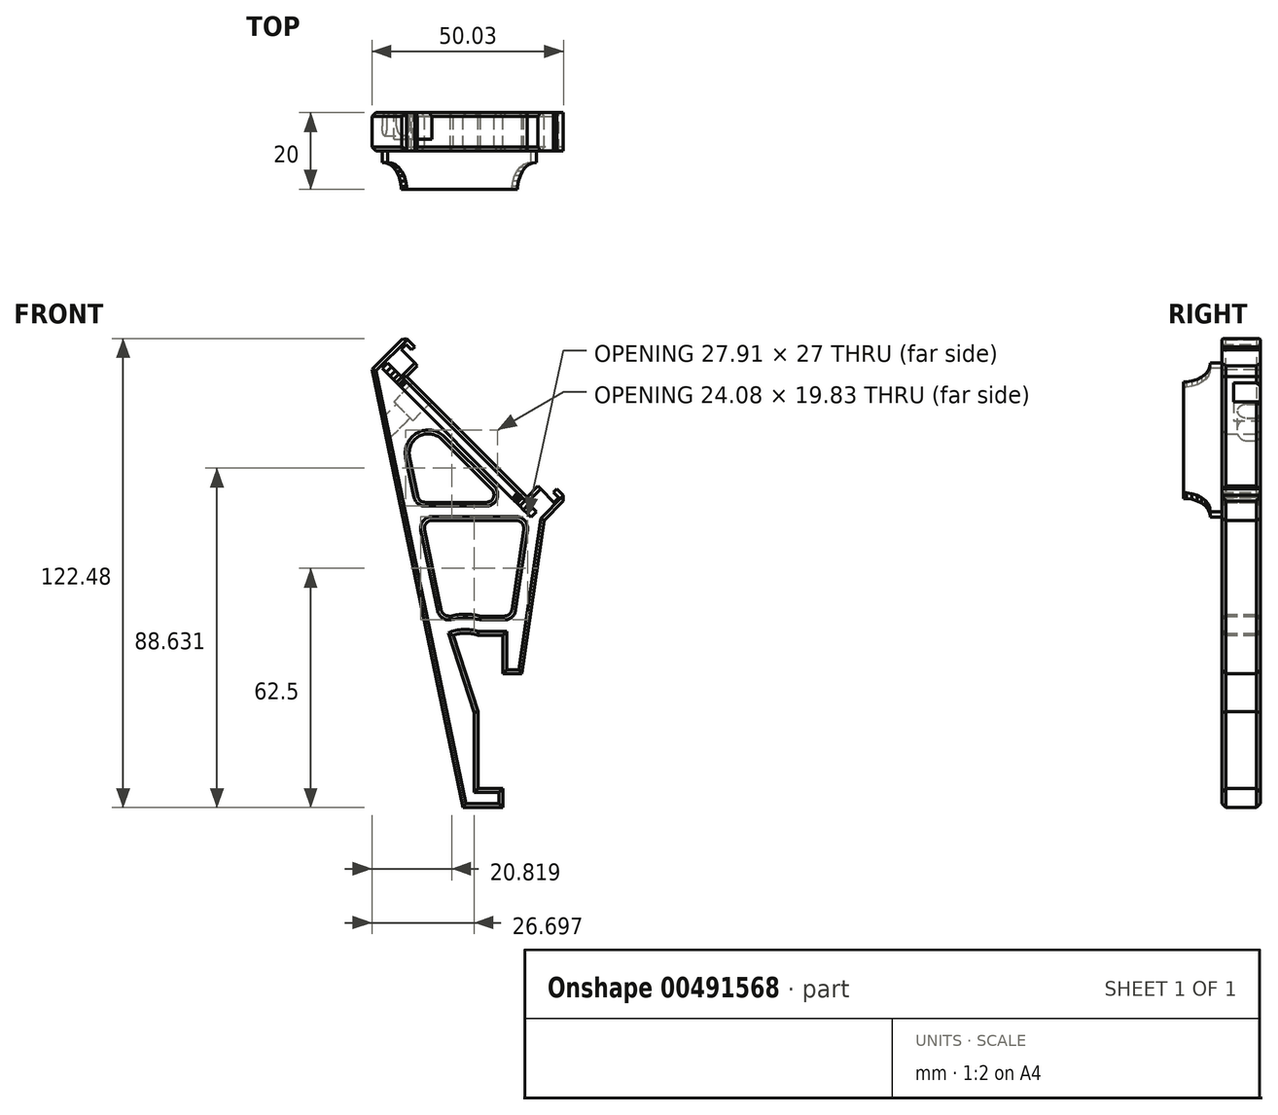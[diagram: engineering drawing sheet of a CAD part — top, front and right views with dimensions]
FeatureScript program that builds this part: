
annotation { "Feature Type Name" : "Feature", "Feature Type Description" : "" }
export const myFeature = defineFeature(function(context is Context, id is Id, definition is map)
    precondition{}
    {
        {
            assignVariable(context, id + "F0", {"name" : "contrastKnobSize", "anyValue" : 7});
        }
        {
            var Q0;
            Q0=qCreatedBy(makeId("Front.planeOp"),FACE);
            var sketch = newSketch(context, id + "F1", { "sketchPlane" : qUnion([Q0])});
            skLineSegment(sketch, "E0", {"start": v(39.1, -18.74) * mm, "end": v(39.1, -17.22) * mm});
            skLineSegment(sketch, "E1", {"start": v(39.1, -17.22) * mm, "end": v(37.38, -15.5) * mm});
            skLineSegment(sketch, "E2", {"start": v(37.38, -15.5) * mm, "end": v(36.53, -16.35) * mm});
            skLineSegment(sketch, "E3", {"start": v(36.53, -16.35) * mm, "end": v(37.94, -17.77) * mm});
            skLineSegment(sketch, "E4", {"start": v(37.94, -17.77) * mm, "end": v(36.67, -19.04) * mm});
            skLineSegment(sketch, "E5", {"start": v(36.67, -19.04) * mm, "end": v(32.43, -14.8) * mm});
            skLineSegment(sketch, "E6", {"start": v(32.43, -14.8) * mm, "end": v(29.6, -17.63) * mm});
            skLineSegment(sketch, "E7", {"start": v(29.6, -17.63) * mm, "end": v(-1.87, 13.84) * mm});
            skLineSegment(sketch, "E8", {"start": v(-1.87, 13.84) * mm, "end": v(0.96, 16.67) * mm});
            skLineSegment(sketch, "E9", {"start": v(0.96, 16.67) * mm, "end": v(-3.28, 20.91) * mm});
            skLineSegment(sketch, "E10", {"start": v(-3.28, 20.91) * mm, "end": v(-2, 22.18) * mm});
            skLineSegment(sketch, "E11", {"start": v(-2, 22.18) * mm, "end": v(-0.6, 20.77) * mm});
            skLineSegment(sketch, "E12", {"start": v(-0.6, 20.77) * mm, "end": v(0.26, 21.62) * mm});
            skLineSegment(sketch, "E13", {"start": v(0.26, 21.62) * mm, "end": v(-1.87, 23.74) * mm});
            skLineSegment(sketch, "E14", {"start": v(-3.15, 23.46) * mm, "end": v(-10.93, 15.68) * mm});
            skLineSegment(sketch, "E15", {"start": v(34.1, -23.74) * mm, "end": v(39.1, -18.74) * mm});
            skLineSegment(sketch, "E16", {"start": v(11.52, -23.74) * mm, "end": v(18.05, -23.74) * mm});
            skLineSegment(sketch, "E17.0", {"start": v(-3.93, -19.02) * mm, "end": v(-3.73, -19.02) * mm});
            skPoint(sketch, "E18.visualSharp", {"position": v(-11.06, -23.74) * mm});
            skLineSegment(sketch, "E18.filletArc", {"start": v(-11.06, -23.74) * mm, "end": v(-11.06, -23.74) * mm});
            skLineSegment(sketch, "E19", {"start": v(34.1, -23.74) * mm, "end": v(34.1, -53.74) * mm, "construction": true});
            skLineSegment(sketch, "E20", {"start": v(34.1, -53.74) * mm, "end": v(34.1, -73.74) * mm, "construction": true});
            skLineSegment(sketch, "E21", {"start": v(7.34, -2.6) * mm, "end": v(20.36, -15.6) * mm});
            skLineSegment(sketch, "E22.trimOffspring", {"start": v(-3.73, -19.02) * mm, "end": v(-3.93, -19.02) * mm, "construction": true});
            skLineSegment(sketch, "E23.trimOffspring", {"start": v(1.05, -17.43) * mm, "end": v(-1.09, -7.15) * mm});
            skLineSegment(sketch, "E24", {"start": v(3, -19.02) * mm, "end": v(18.94, -19.02) * mm});
            skPoint(sketch, "E25.visualSharp", {"position": v(1.38, -19.02) * mm});
            skArc(sketch, "E25.filletArc", {"start": v(1.05, -17.43) * mm, "mid": v(1.74, -18.58) * mm, "end": v(3, -19.02) * mm});
            skPoint(sketch, "E26.visualSharp", {"position": v(23.77, -19.02) * mm});
            skArc(sketch, "E26.filletArc", {"start": v(18.94, -19.02) * mm, "mid": v(20.8, -17.79) * mm, "end": v(20.36, -15.6) * mm});
            skLineSegment(sketch, "E27.trimOffspring", {"start": v(23.05, -23.74) * mm, "end": v(26.73, -23.74) * mm});
            skPoint(sketch, "E28.0.midPoint", {"position": v(0, 0.45) * mm});
            skLineSegment(sketch, "E29", {"start": v(-1.87, 23.74) * mm, "end": v(-3.15, 23.46) * mm});
            skArc(sketch, "E30.filletArc", {"start": v(7.34, -2.6) * mm, "mid": v(1.43, -1.73) * mm, "end": v(-1.09, -7.15) * mm});
            skLineSegment(sketch, "E31", {"start": v(23.05, -23.74) * mm, "end": v(18.05, -23.74) * mm});
            skLineSegment(sketch, "E32", {"start": v(11.52, -23.74) * mm, "end": v(5.02, -23.74) * mm});
            skLineSegment(sketch, "E33", {"start": v(5.02, -23.74) * mm, "end": v(4.81, -23.74) * mm});
            skLineSegment(sketch, "E34.trimOffspring", {"start": v(-2.75, -23.74) * mm, "end": v(-10.93, 15.68) * mm});
            skPoint(sketch, "E35.start.orphan", {"position": v(11.52, -53.74) * mm});
            skLineSegment(sketch, "E36", {"start": v(34.1, -73.74) * mm, "end": v(34.1, -93.74) * mm, "construction": true});
            skLineSegment(sketch, "E37", {"start": v(-2.75, -23.74) * mm, "end": v(12.81, -98.74) * mm});
            skLineSegment(sketch, "E38", {"start": v(34.1, -93.74) * mm, "end": v(16.77, -93.74) * mm, "construction": true});
            skLineSegment(sketch, "E39", {"start": v(16.77, -93.74) * mm, "end": v(16.77, -73.74) * mm});
            skLineSegment(sketch, "E40", {"start": v(16.77, -73.74) * mm, "end": v(10.28, -53.74) * mm});
            skPoint(sketch, "E41.orphan", {"position": v(16.77, -53.74) * mm});
            skLineSegment(sketch, "E42", {"start": v(16.77, -53.74) * mm, "end": v(23.27, -53.74) * mm});
            skLineSegment(sketch, "E43", {"start": v(23.27, -53.74) * mm, "end": v(23.27, -63.74) * mm});
            skLineSegment(sketch, "E44", {"start": v(23.27, -63.74) * mm, "end": v(28.27, -63.74) * mm});
            skLineSegment(sketch, "E45", {"start": v(28.27, -63.74) * mm, "end": v(34.1, -23.74) * mm});
            skArc(sketch, "E46", {"start": v(16.77, -53.74) * mm, "mid": v(13.52, -53.23) * mm, "end": v(10.28, -53.74) * mm});
            skLineSegment(sketch, "E47", {"start": v(16.77, -93.74) * mm, "end": v(23.27, -93.74) * mm});
            skLineSegment(sketch, "E48", {"start": v(23.27, -93.74) * mm, "end": v(23.27, -98.74) * mm});
            skLineSegment(sketch, "E49", {"start": v(23.27, -98.74) * mm, "end": v(12.81, -98.74) * mm});
            skLineSegment(sketch, "E50.0", {"start": v(25.65, -47.03) * mm, "end": v(28.7, -26.03) * mm});
            skLineSegment(sketch, "E51.0", {"start": v(2.85, -26.15) * mm, "end": v(7.21, -47.15) * mm});
            skLineSegment(sketch, "E52.trimOffspring", {"start": v(16.77, -93.23) * mm, "end": v(17.7, -97.72) * mm, "construction": true});
            skPoint(sketch, "E53.orphan", {"position": v(-11.06, -53.74) * mm});
            skLineSegment(sketch, "E54.trimOffspring", {"start": v(23.67, -48.74) * mm, "end": v(17.49, -48.74) * mm});
            skLineSegment(sketch, "E55.trimOffspring", {"start": v(24.68, -53.74) * mm, "end": v(8.58, -53.74) * mm, "construction": true});
            skArc(sketch, "E56.0", {"start": v(17.49, -48.74) * mm, "mid": v(13.52, -48.23) * mm, "end": v(9.56, -48.74) * mm});
            skLineSegment(sketch, "E57.trimOffspring", {"start": v(9.56, -48.74) * mm, "end": v(9.17, -48.74) * mm});
            skPoint(sketch, "E58.visualSharp", {"position": v(29.04, -23.74) * mm});
            skArc(sketch, "E58.filletArc", {"start": v(28.7, -26.03) * mm, "mid": v(28.24, -24.43) * mm, "end": v(26.73, -23.74) * mm});
            skPoint(sketch, "E59.visualSharp", {"position": v(2.36, -23.74) * mm});
            skArc(sketch, "E59.filletArc", {"start": v(4.81, -23.74) * mm, "mid": v(3.26, -24.48) * mm, "end": v(2.85, -26.15) * mm});
            skPoint(sketch, "E60.visualSharp", {"position": v(25.4, -48.74) * mm});
            skArc(sketch, "E60.filletArc", {"start": v(23.67, -48.74) * mm, "mid": v(24.98, -48.25) * mm, "end": v(25.65, -47.03) * mm});
            skPoint(sketch, "E61.visualSharp", {"position": v(7.54, -48.74) * mm});
            skArc(sketch, "E61.filletArc", {"start": v(7.21, -47.15) * mm, "mid": v(7.9, -48.3) * mm, "end": v(9.17, -48.74) * mm});
            skSolve(sketch);
        }
        {
            var Q0;
            Q0=makeQuery(id+"F1.imprint","IMPRINT",FACE,{"disambiguationData":[TD([[makeQuery(id+"F1.imprint","IMPRINT",EDGE,{"derivedFrom":sQuery(id+"F1.wireOp",EDGE,"E0")}),1.0]])]});
            extrude(context, id + "F2", {"entities" : qUnion([Q0]), "depth" : 10 * mm, "offsetDistance" : 25 * mm});
        }
        {
            var Q0;
            Q0=makeQuery(id+"F2.opExtrude","SWEPT_FACE",FACE,{"disambiguationData":[OSD([sQuery(id+"F1.wireOp",EDGE,"E7")])]});
            var sketch = newSketch(context, id + "F3", { "sketchPlane" : qUnion([Q0])});
            skLineSegment(sketch, "E62", {"start": v(-9.27, -29.2) * mm, "end": v(-7.84, -29.5) * mm});
            skLineSegment(sketch, "E63", {"start": v(-7.84, -29.5) * mm, "end": v(-6.5, -30.1) * mm});
            skLineSegment(sketch, "E64", {"start": v(-6.5, -30.1) * mm, "end": v(-5.32, -30.96) * mm});
            skLineSegment(sketch, "E65", {"start": v(-5.32, -30.96) * mm, "end": v(-4.34, -32.05) * mm});
            skLineSegment(sketch, "E66", {"start": v(-4.34, -32.05) * mm, "end": v(-3.6, -33.32) * mm});
            skLineSegment(sketch, "E67", {"start": v(-3.6, -33.32) * mm, "end": v(-3.15, -34.7) * mm});
            skLineSegment(sketch, "E68", {"start": v(-3.15, -34.7) * mm, "end": v(-3, -36.16) * mm});
            skLineSegment(sketch, "E69", {"start": v(-3, -36.16) * mm, "end": v(0, -36.16) * mm});
            skLineSegment(sketch, "E70", {"start": v(0, -36.16) * mm, "end": v(0, -39.16) * mm});
            skLineSegment(sketch, "E71", {"start": v(0, -39.16) * mm, "end": v(10, -39.16) * mm});
            skLineSegment(sketch, "E72", {"start": v(10, -39.16) * mm, "end": v(10, 39.16) * mm});
            skLineSegment(sketch, "E73", {"start": v(10, 39.16) * mm, "end": v(7.98, 39.16) * mm});
            skLineSegment(sketch, "E74", {"start": v(7.98, 39.16) * mm, "end": v(7.98, 39.03) * mm});
            skLineSegment(sketch, "E75", {"start": v(7.98, 39.03) * mm, "end": v(7.87, 38.8) * mm});
            skLineSegment(sketch, "E76", {"start": v(7.87, 38.8) * mm, "end": v(7.85, 38.75) * mm});
            skLineSegment(sketch, "E77", {"start": v(7.85, 38.75) * mm, "end": v(7.6, 38.4) * mm});
            skLineSegment(sketch, "E78", {"start": v(7.6, 38.4) * mm, "end": v(7.23, 38.1) * mm});
            skLineSegment(sketch, "E79", {"start": v(7.23, 38.1) * mm, "end": v(6.92, 37.94) * mm});
            skLineSegment(sketch, "E80", {"start": v(6.92, 37.94) * mm, "end": v(6.76, 37.83) * mm});
            skLineSegment(sketch, "E81", {"start": v(6.76, 37.83) * mm, "end": v(6.22, 37.6) * mm});
            skLineSegment(sketch, "E82", {"start": v(6.22, 37.6) * mm, "end": v(5.62, 37.46) * mm});
            skLineSegment(sketch, "E83", {"start": v(5.62, 37.46) * mm, "end": v(5, 37.4) * mm});
            skLineSegment(sketch, "E84", {"start": v(5, 37.4) * mm, "end": v(4.38, 37.46) * mm});
            skLineSegment(sketch, "E85", {"start": v(4.38, 37.46) * mm, "end": v(3.78, 37.6) * mm});
            skLineSegment(sketch, "E86", {"start": v(3.78, 37.6) * mm, "end": v(3.24, 37.83) * mm});
            skLineSegment(sketch, "E87", {"start": v(3.24, 37.83) * mm, "end": v(3.08, 37.94) * mm});
            skLineSegment(sketch, "E88", {"start": v(3.08, 37.94) * mm, "end": v(2.77, 38.1) * mm});
            skLineSegment(sketch, "E89", {"start": v(2.77, 38.1) * mm, "end": v(2.4, 38.4) * mm});
            skLineSegment(sketch, "E90", {"start": v(2.4, 38.4) * mm, "end": v(2.15, 38.75) * mm});
            skLineSegment(sketch, "E91", {"start": v(2.15, 38.75) * mm, "end": v(2.13, 38.8) * mm});
            skLineSegment(sketch, "E92", {"start": v(2.13, 38.8) * mm, "end": v(2.02, 39.03) * mm});
            skLineSegment(sketch, "E93", {"start": v(2.02, 39.03) * mm, "end": v(2.02, 39.16) * mm});
            skLineSegment(sketch, "E94", {"start": v(2.02, 39.16) * mm, "end": v(0, 39.16) * mm});
            skLineSegment(sketch, "E95", {"start": v(0, 39.16) * mm, "end": v(0, 18.84) * mm});
            skLineSegment(sketch, "E96", {"start": v(0, 18.84) * mm, "end": v(-3, 18.84) * mm});
            skLineSegment(sketch, "E97", {"start": v(-3, 18.84) * mm, "end": v(-3.15, 17.38) * mm});
            skLineSegment(sketch, "E98", {"start": v(-3.15, 17.38) * mm, "end": v(-3.6, 15.99) * mm});
            skLineSegment(sketch, "E99", {"start": v(-3.6, 15.99) * mm, "end": v(-4.34, 14.72) * mm});
            skLineSegment(sketch, "E100", {"start": v(-4.34, 14.72) * mm, "end": v(-5.32, 13.63) * mm});
            skLineSegment(sketch, "E101", {"start": v(-5.32, 13.63) * mm, "end": v(-6.5, 12.77) * mm});
            skLineSegment(sketch, "E102", {"start": v(-6.5, 12.77) * mm, "end": v(-7.84, 12.18) * mm});
            skLineSegment(sketch, "E103", {"start": v(-7.84, 12.18) * mm, "end": v(-9.27, 11.87) * mm});
            skLineSegment(sketch, "E104", {"start": v(-9.27, 11.87) * mm, "end": v(-10, 11.87) * mm});
            skLineSegment(sketch, "E105", {"start": v(-10, 11.87) * mm, "end": v(-10, -29.2) * mm});
            skLineSegment(sketch, "E106", {"start": v(-10, -29.2) * mm, "end": v(-9.27, -29.2) * mm});
            skLineSegment(sketch, "E107", {"start": v(0, -36.16) * mm, "end": v(0, 18.84) * mm});
            skSolve(sketch);
        }
        {
            var Q0;
            Q0=makeQuery(id+"F3.imprint","IMPRINT",FACE,{"disambiguationData":[TD([[makeQuery(id+"F3.imprint","IMPRINT",EDGE,{"derivedFrom":sQuery(id+"F3.wireOp",EDGE,"E62")}),1.0]])]});
            var Q1;
            {var subQ3=sQuery(id+"F3.wireOp",EDGE,"E96");Q1=makeQuery(id+"F3.imprint","IMPRINT",FACE,{"disambiguationData":[TD([[makeQuery(id+"F3.imprint","IMPRINT",EDGE,{"derivedFrom":subQ3}),1.0]])]});}
            var Q2;
            {var subQ4=sQuery(id+"F3.wireOp",EDGE,"E68");Q2=makeQuery(id+"F3.imprint","IMPRINT",FACE,{"disambiguationData":[TD([[makeQuery(id+"F3.imprint","IMPRINT",EDGE,{"derivedFrom":subQ4}),1.0]])]});}
            extrude(context, id + "F4", {"entities" : qUnion([Q0, Q1, Q2]), "depth" : 2 * mm, "offsetDistance" : 25 * mm});
        }
        {
            var Q0;
            Q0=makeQuery(id+"F2.opExtrude","CAP_FACE",FACE,{"disambiguationData":[OSD([sQuery(id+"F1.wireOp",EDGE,"E0"),sQuery(id+"F1.wireOp",EDGE,"E1"),sQuery(id+"F1.wireOp",EDGE,"E2"),sQuery(id+"F1.wireOp",EDGE,"E3"),sQuery(id+"F1.wireOp",EDGE,"E4"),sQuery(id+"F1.wireOp",EDGE,"E5"),sQuery(id+"F1.wireOp",EDGE,"E6"),sQuery(id+"F1.wireOp",EDGE,"E7"),sQuery(id+"F1.wireOp",EDGE,"E8"),sQuery(id+"F1.wireOp",EDGE,"E9"),sQuery(id+"F1.wireOp",EDGE,"E10"),sQuery(id+"F1.wireOp",EDGE,"E11"),sQuery(id+"F1.wireOp",EDGE,"E12"),sQuery(id+"F1.wireOp",EDGE,"E13"),sQuery(id+"F1.wireOp",EDGE,"3a1ae434-b03a-431a-9713-1d6dea57bce0"),sQuery(id+"F1.wireOp",EDGE,"E14"),sQuery(id+"F1.wireOp",EDGE,"E15"),sQuery(id+"F1.wireOp",EDGE,"E16"),sQuery(id+"F1.wireOp",EDGE,"E35"),sQuery(id+"F1.wireOp",EDGE,"3y1IdGgq-BFH6-ljYC-aM2y-RlinSgV9mvII"),sQuery(id+"F1.wireOp",EDGE,"z6kHnCYS-EehM-PqFy-aRZG-R0Hd5bpDfOqk"),sQuery(id+"F1.wireOp",EDGE,"ky2B1AaY-Og2m-jc2H-LCDa-p9N1nHVHlabs"),sQuery(id+"F1.wireOp",EDGE,"TqFosptJ-e80p-NSia-VRGU-4potEBLNdm0S"),sQuery(id+"F1.wireOp",EDGE,"Vc4PoYxX-D6Pj-s6fX-x5NK-R8lTQmO3Xmnw"),sQuery(id+"F1.wireOp",EDGE,"DqzT9wzE-QKBd-hKXL-xd2i-dLmxpIQpI03c"),sQuery(id+"F1.wireOp",EDGE,"mqRVrvuD-t7La-ja7Q-XqRT-M8NbmPeLfjHI"),sQuery(id+"F1.wireOp",EDGE,"Aao6JbBj-ixHZ-LHBj-1GMs-VehlcfEAaExJ"),sQuery(id+"F1.wireOp",EDGE,"XXJIcc4o-OTew-1mbU-SmsV-49a9MDvK9wcg"),sQuery(id+"F1.wireOp",EDGE,"15d13afc-9ba3-4549-bfcd-cc3ab7ef1af9.trimOffspring"),sQuery(id+"F1.wireOp",EDGE,"E21"),sQuery(id+"F1.wireOp",EDGE,"E23.trimOffspring"),sQuery(id+"F1.wireOp",EDGE,"E24"),sQuery(id+"F1.wireOp",EDGE,"fc2781de-b2b6-4d6d-b4a7-d93c8ebd055b.filletArc"),sQuery(id+"F1.wireOp",EDGE,"E25.filletArc"),sQuery(id+"F1.wireOp",EDGE,"E26.filletArc"),sQuery(id+"F1.wireOp",EDGE,"E27.trimOffspring")])],"isStart":true});
            var sketch = newSketch(context, id + "F5", { "sketchPlane" : qUnion([Q0])});
            skLineSegment(sketch, "E108.0.0", {"start": v(-31.56, -19.58) * mm, "end": v(7.33, 19.3) * mm, "construction": true});
            skLineSegment(sketch, "E108.0.1", {"start": v(7.33, 19.3) * mm, "end": v(5.92, 20.72) * mm, "construction": true});
            skLineSegment(sketch, "E108.0.2", {"start": v(5.92, 20.72) * mm, "end": v(-32.97, -18.17) * mm, "construction": true});
            skLineSegment(sketch, "E108.0.3", {"start": v(-32.97, -18.17) * mm, "end": v(-31.56, -19.58) * mm, "construction": true});
            skLineSegment(sketch, "E109.0", {"start": v(-39.1, -18.74) * mm, "end": v(-39.1, -18.74) * mm});
            skLineSegment(sketch, "E110", {"start": v(-31.56, -19.58) * mm, "end": v(-30.85, -20.3) * mm, "construction": true});
            skLineSegment(sketch, "E111", {"start": v(-34.9, -22.93) * mm, "end": v(-32.78, -20.8) * mm, "construction": true});
            skLineSegment(sketch, "E112", {"start": v(-32.78, -20.8) * mm, "end": v(-31.56, -19.58) * mm, "construction": true});
            skSolve(sketch);
        }
        {
            var Q0;
            Q0=makeQuery(id+"F4.opExtrude","SWEPT_BODY",BODY,{"disambiguationData":[OSD([sQuery(id+"F3.wireOp",EDGE,"E62"),sQuery(id+"F3.wireOp",EDGE,"E63"),sQuery(id+"F3.wireOp",EDGE,"E64"),sQuery(id+"F3.wireOp",EDGE,"E65"),sQuery(id+"F3.wireOp",EDGE,"E66"),sQuery(id+"F3.wireOp",EDGE,"E67"),sQuery(id+"F3.wireOp",EDGE,"E68"),sQuery(id+"F3.wireOp",EDGE,"E69"),sQuery(id+"F3.wireOp",EDGE,"E96"),sQuery(id+"F3.wireOp",EDGE,"E97"),sQuery(id+"F3.wireOp",EDGE,"E98"),sQuery(id+"F3.wireOp",EDGE,"E99"),sQuery(id+"F3.wireOp",EDGE,"E100"),sQuery(id+"F3.wireOp",EDGE,"E101"),sQuery(id+"F3.wireOp",EDGE,"E102"),sQuery(id+"F3.wireOp",EDGE,"E103"),sQuery(id+"F3.wireOp",EDGE,"E104"),sQuery(id+"F3.wireOp",EDGE,"E105"),sQuery(id+"F3.wireOp",EDGE,"E106"),sQuery(id+"F3.wireOp",EDGE,"E107")])]});
            var Q1;
            Q1=sQuery(id+"F5.wireOp",EDGE,"E112");
            transform(context, id + "F6", {"entities" : qUnion([Q0]), "transformType" : TransformType.TRANSLATION_ENTITY, "oppositeDirectionEntity" : true, "transformLine" : qUnion([Q1]), "makeCopy" : false});
        }
        {
            var Q0;
            Q0=makeQuery(id+"F4.opExtrude","SWEPT_BODY",BODY,{"disambiguationData":[OSD([sQuery(id+"F3.wireOp",EDGE,"E62"),sQuery(id+"F3.wireOp",EDGE,"E63"),sQuery(id+"F3.wireOp",EDGE,"E64"),sQuery(id+"F3.wireOp",EDGE,"E65"),sQuery(id+"F3.wireOp",EDGE,"E66"),sQuery(id+"F3.wireOp",EDGE,"E67"),sQuery(id+"F3.wireOp",EDGE,"E68"),sQuery(id+"F3.wireOp",EDGE,"E69"),sQuery(id+"F3.wireOp",EDGE,"E96"),sQuery(id+"F3.wireOp",EDGE,"E97"),sQuery(id+"F3.wireOp",EDGE,"E98"),sQuery(id+"F3.wireOp",EDGE,"E99"),sQuery(id+"F3.wireOp",EDGE,"E100"),sQuery(id+"F3.wireOp",EDGE,"E101"),sQuery(id+"F3.wireOp",EDGE,"E102"),sQuery(id+"F3.wireOp",EDGE,"E103"),sQuery(id+"F3.wireOp",EDGE,"E104"),sQuery(id+"F3.wireOp",EDGE,"E105"),sQuery(id+"F3.wireOp",EDGE,"E106"),sQuery(id+"F3.wireOp",EDGE,"E107")])]});
            var Q1;
            Q1=makeQuery(id+"F2.opExtrude","SWEPT_EDGE",EDGE,{"disambiguationData":[OSD([sQuery(id+"F1.wireOp",EDGE,"E5"),sQuery(id+"F1.wireOp",EDGE,"E6")])]});
            transform(context, id + "F7", {"entities" : qUnion([Q0]), "transformType" : TransformType.TRANSLATION_ENTITY, "oppositeDirectionEntity" : true, "transformLine" : qUnion([Q1]), "makeCopy" : false});
        }
        {
            var Q0;
            Q0=makeQuery(id+"F4.opExtrude","SWEPT_BODY",BODY,{"disambiguationData":[OSD([sQuery(id+"F3.wireOp",EDGE,"E62"),sQuery(id+"F3.wireOp",EDGE,"E63"),sQuery(id+"F3.wireOp",EDGE,"E64"),sQuery(id+"F3.wireOp",EDGE,"E65"),sQuery(id+"F3.wireOp",EDGE,"E66"),sQuery(id+"F3.wireOp",EDGE,"E67"),sQuery(id+"F3.wireOp",EDGE,"E68"),sQuery(id+"F3.wireOp",EDGE,"E69"),sQuery(id+"F3.wireOp",EDGE,"E96"),sQuery(id+"F3.wireOp",EDGE,"E97"),sQuery(id+"F3.wireOp",EDGE,"E98"),sQuery(id+"F3.wireOp",EDGE,"E99"),sQuery(id+"F3.wireOp",EDGE,"E100"),sQuery(id+"F3.wireOp",EDGE,"E101"),sQuery(id+"F3.wireOp",EDGE,"E102"),sQuery(id+"F3.wireOp",EDGE,"E103"),sQuery(id+"F3.wireOp",EDGE,"E104"),sQuery(id+"F3.wireOp",EDGE,"E105"),sQuery(id+"F3.wireOp",EDGE,"E106"),sQuery(id+"F3.wireOp",EDGE,"E107")])]});
            var Q1;
            Q1=makeQuery(id+"F4.opExtrude","SWEPT_EDGE",EDGE,{"disambiguationData":[OSD([sQuery(id+"F3.wireOp",EDGE,"E104"),sQuery(id+"F3.wireOp",EDGE,"E105")])]});
            transform(context, id + "F8", {"entities" : qUnion([Q0]), "transformType" : TransformType.TRANSLATION_ENTITY, "oppositeDirectionEntity" : false, "transformLine" : qUnion([Q1]), "makeCopy" : false});
        }
        {
            var Q0;
            Q0=makeQuery(id+"F2.opExtrude","CAP_FACE",FACE,{"disambiguationData":[OSD([sQuery(id+"F1.wireOp",EDGE,"E0"),sQuery(id+"F1.wireOp",EDGE,"E1"),sQuery(id+"F1.wireOp",EDGE,"E2"),sQuery(id+"F1.wireOp",EDGE,"E3"),sQuery(id+"F1.wireOp",EDGE,"E4"),sQuery(id+"F1.wireOp",EDGE,"E5"),sQuery(id+"F1.wireOp",EDGE,"E6"),sQuery(id+"F1.wireOp",EDGE,"E7"),sQuery(id+"F1.wireOp",EDGE,"E8"),sQuery(id+"F1.wireOp",EDGE,"E9"),sQuery(id+"F1.wireOp",EDGE,"E10"),sQuery(id+"F1.wireOp",EDGE,"E11"),sQuery(id+"F1.wireOp",EDGE,"E12"),sQuery(id+"F1.wireOp",EDGE,"E13"),sQuery(id+"F1.wireOp",EDGE,"E14"),sQuery(id+"F1.wireOp",EDGE,"E15"),sQuery(id+"F1.wireOp",EDGE,"E16"),sQuery(id+"F1.wireOp",EDGE,"E35"),sQuery(id+"F1.wireOp",EDGE,"3y1IdGgq-BFH6-ljYC-aM2y-RlinSgV9mvII"),sQuery(id+"F1.wireOp",EDGE,"z6kHnCYS-EehM-PqFy-aRZG-R0Hd5bpDfOqk"),sQuery(id+"F1.wireOp",EDGE,"ky2B1AaY-Og2m-jc2H-LCDa-p9N1nHVHlabs"),sQuery(id+"F1.wireOp",EDGE,"TqFosptJ-e80p-NSia-VRGU-4potEBLNdm0S"),sQuery(id+"F1.wireOp",EDGE,"Vc4PoYxX-D6Pj-s6fX-x5NK-R8lTQmO3Xmnw"),sQuery(id+"F1.wireOp",EDGE,"DqzT9wzE-QKBd-hKXL-xd2i-dLmxpIQpI03c"),sQuery(id+"F1.wireOp",EDGE,"mqRVrvuD-t7La-ja7Q-XqRT-M8NbmPeLfjHI"),sQuery(id+"F1.wireOp",EDGE,"Aao6JbBj-ixHZ-LHBj-1GMs-VehlcfEAaExJ"),sQuery(id+"F1.wireOp",EDGE,"XXJIcc4o-OTew-1mbU-SmsV-49a9MDvK9wcg"),sQuery(id+"F1.wireOp",EDGE,"15d13afc-9ba3-4549-bfcd-cc3ab7ef1af9.trimOffspring"),sQuery(id+"F1.wireOp",EDGE,"E27.trimOffspring"),sQuery(id+"F1.wireOp",EDGE,"aaa1e90f-5d83-49da-a6ae-3bc370373b5e.0"),sQuery(id+"F1.wireOp",EDGE,"aaa1e90f-5d83-49da-a6ae-3bc370373b5e.1"),sQuery(id+"F1.wireOp",EDGE,"aaa1e90f-5d83-49da-a6ae-3bc370373b5e.2"),sQuery(id+"F1.wireOp",EDGE,"aaa1e90f-5d83-49da-a6ae-3bc370373b5e.3"),sQuery(id+"F1.wireOp",EDGE,"aaa1e90f-5d83-49da-a6ae-3bc370373b5e.4"),sQuery(id+"F1.wireOp",EDGE,"aaa1e90f-5d83-49da-a6ae-3bc370373b5e.5"),sQuery(id+"F1.wireOp",EDGE,"E28.0"),sQuery(id+"F1.wireOp",EDGE,"E28.1"),sQuery(id+"F1.wireOp",EDGE,"E28.2"),sQuery(id+"F1.wireOp",EDGE,"E28.3"),sQuery(id+"F1.wireOp",EDGE,"E28.4"),sQuery(id+"F1.wireOp",EDGE,"E28.5"),sQuery(id+"F1.wireOp",EDGE,"e371573f-29d2-429a-a5fa-f8348fbc9dea.0"),sQuery(id+"F1.wireOp",EDGE,"e371573f-29d2-429a-a5fa-f8348fbc9dea.1"),sQuery(id+"F1.wireOp",EDGE,"e371573f-29d2-429a-a5fa-f8348fbc9dea.2"),sQuery(id+"F1.wireOp",EDGE,"e371573f-29d2-429a-a5fa-f8348fbc9dea.3"),sQuery(id+"F1.wireOp",EDGE,"e371573f-29d2-429a-a5fa-f8348fbc9dea.4"),sQuery(id+"F1.wireOp",EDGE,"e371573f-29d2-429a-a5fa-f8348fbc9dea.5"),sQuery(id+"F1.wireOp",EDGE,"a4f73cd4-313a-4532-9c9a-ea7ef1a286e2.0"),sQuery(id+"F1.wireOp",EDGE,"a4f73cd4-313a-4532-9c9a-ea7ef1a286e2.1"),sQuery(id+"F1.wireOp",EDGE,"a4f73cd4-313a-4532-9c9a-ea7ef1a286e2.2"),sQuery(id+"F1.wireOp",EDGE,"a4f73cd4-313a-4532-9c9a-ea7ef1a286e2.3"),sQuery(id+"F1.wireOp",EDGE,"a4f73cd4-313a-4532-9c9a-ea7ef1a286e2.4"),sQuery(id+"F1.wireOp",EDGE,"a4f73cd4-313a-4532-9c9a-ea7ef1a286e2.5"),sQuery(id+"F1.wireOp",EDGE,"E29")])],"isStart":true});
            var sketch = newSketch(context, id + "F9", { "sketchPlane" : qUnion([Q0])});
            skLineSegment(sketch, "E113", {"start": v(0.25, 12.22) * mm, "end": v(7.32, 19.3) * mm, "construction": true});
            skLineSegment(sketch, "E114", {"start": v(0.25, 12.22) * mm, "end": v(5.2, 7.27) * mm});
            skLineSegment(sketch, "E115", {"start": v(5.2, 7.27) * mm, "end": v(0.25, 2.32) * mm});
            skLineSegment(sketch, "E116", {"start": v(0.25, 2.32) * mm, "end": v(-4.7, 7.27) * mm});
            skSolve(sketch);
        }
        {
            var Q0;
            {var subQ0=sQuery(id+"F9.wireOp",EDGE,"E114");Q0=makeQuery(id+"F9.imprint","IMPRINT",FACE,{"disambiguationData":[TD([[makeQuery(id+"F9.imprint","IMPRINT",EDGE,{"derivedFrom":subQ0}),-1.0]])]});}
            var Q1;
            Q1=makeQuery(id+"F9.imprint","IMPRINT",FACE,{"disambiguationData":[TD([[makeQuery(id+"F9.imprint","IMPRINT",EDGE,{"derivedFrom":sQuery(id+"F9.wireOp",EDGE,"8zuXLHW3-z8Jz-yU3E-51QL-163BtuiGQZgh")}),1.0]])]});
            extrude(context, id + "F10", {"entities" : qUnion([Q0, Q1]), "operationType" : NewBodyOperationType.REMOVE, "oppositeDirection" : true, "depth" : (getVariable(context, 'contrastKnobSize')) * mm, "offsetDistance" : 25 * mm});
        }
        {
            var Q0;
            Q0=makeQuery(id+"F4.opExtrude","SWEPT_BODY",BODY,{"disambiguationData":[OSD([sQuery(id+"F3.wireOp",EDGE,"E62"),sQuery(id+"F3.wireOp",EDGE,"E63"),sQuery(id+"F3.wireOp",EDGE,"E64"),sQuery(id+"F3.wireOp",EDGE,"E65"),sQuery(id+"F3.wireOp",EDGE,"E66"),sQuery(id+"F3.wireOp",EDGE,"E67"),sQuery(id+"F3.wireOp",EDGE,"E68"),sQuery(id+"F3.wireOp",EDGE,"E69"),sQuery(id+"F3.wireOp",EDGE,"E96"),sQuery(id+"F3.wireOp",EDGE,"E97"),sQuery(id+"F3.wireOp",EDGE,"E98"),sQuery(id+"F3.wireOp",EDGE,"E99"),sQuery(id+"F3.wireOp",EDGE,"E100"),sQuery(id+"F3.wireOp",EDGE,"E101"),sQuery(id+"F3.wireOp",EDGE,"E102"),sQuery(id+"F3.wireOp",EDGE,"E103"),sQuery(id+"F3.wireOp",EDGE,"E104"),sQuery(id+"F3.wireOp",EDGE,"E105"),sQuery(id+"F3.wireOp",EDGE,"E106"),sQuery(id+"F3.wireOp",EDGE,"E107")])]});
            var Q1;
            Q1=makeQuery(id+"F4.opExtrude","SWEPT_EDGE",EDGE,{"disambiguationData":[OSD([sQuery(id+"F3.wireOp",EDGE,"E104"),sQuery(id+"F3.wireOp",EDGE,"E105")])]});
            transform(context, id + "F11", {"entities" : qUnion([Q0]), "transformType" : TransformType.TRANSLATION_DISTANCE, "transformDirection" : qUnion([Q1]), "distance" : 1 * mm, "makeCopy" : false});
        }
        {
            var Q0;
            Q0=makeQuery(id+"F2.opExtrude","CAP_EDGE",EDGE,{"disambiguationData":[OSD([sQuery(id+"F1.wireOp",EDGE,"E21")])],"isStart":false});
            var Q1;
            Q1=makeQuery(id+"F2.opExtrude","CAP_EDGE",EDGE,{"disambiguationData":[OSD([sQuery(id+"F1.wireOp",EDGE,"E21")])],"isStart":true});
            var Q2;
            Q2=makeQuery(id+"F2.opExtrude","CAP_EDGE",EDGE,{"disambiguationData":[OSD([sQuery(id+"F1.wireOp",EDGE,"XXJIcc4o-OTew-1mbU-SmsV-49a9MDvK9wcg")])],"isStart":false});
            var Q3;
            Q3=makeQuery(id+"F2.opExtrude","CAP_EDGE",EDGE,{"disambiguationData":[OSD([sQuery(id+"F1.wireOp",EDGE,"XXJIcc4o-OTew-1mbU-SmsV-49a9MDvK9wcg")])],"isStart":true});
            var Q4;
            Q4=makeQuery(id+"F2.opExtrude","CAP_EDGE",EDGE,{"disambiguationData":[OSD([sQuery(id+"F1.wireOp",EDGE,"E7")])],"isStart":false});
            var Q5;
            Q5=makeQuery(id+"F2.opExtrude","CAP_EDGE",EDGE,{"disambiguationData":[OSD([sQuery(id+"F1.wireOp",EDGE,"E7")])],"isStart":true});
            var Q6;
            Q6=makeQuery(id+"F2.opExtrude","CAP_EDGE",EDGE,{"disambiguationData":[OSD([sQuery(id+"F1.wireOp",EDGE,"3y1IdGgq-BFH6-ljYC-aM2y-RlinSgV9mvII")])],"isStart":false});
            var Q7;
            Q7=makeQuery(id+"F2.opExtrude","CAP_EDGE",EDGE,{"disambiguationData":[OSD([sQuery(id+"F1.wireOp",EDGE,"E35")])],"isStart":false});
            var Q8;
            Q8=makeQuery(id+"F2.opExtrude","CAP_EDGE",EDGE,{"disambiguationData":[OSD([sQuery(id+"F1.wireOp",EDGE,"E35")])],"isStart":true});
            var Q9;
            Q9=makeQuery(id+"F2.opExtrude","CAP_EDGE",EDGE,{"disambiguationData":[OSD([sQuery(id+"F1.wireOp",EDGE,"3y1IdGgq-BFH6-ljYC-aM2y-RlinSgV9mvII")])],"isStart":true});
            var Q10;
            Q10=makeQuery(id+"F2.opExtrude","CAP_EDGE",EDGE,{"disambiguationData":[OSD([sQuery(id+"F1.wireOp",EDGE,"TqFosptJ-e80p-NSia-VRGU-4potEBLNdm0S"),sQuery(id+"F1.wireOp",EDGE,"Vc4PoYxX-D6Pj-s6fX-x5NK-R8lTQmO3Xmnw")])],"isStart":false});
            var Q11;
            Q11=makeQuery(id+"F2.opExtrude","CAP_EDGE",EDGE,{"disambiguationData":[OSD([sQuery(id+"F1.wireOp",EDGE,"z6kHnCYS-EehM-PqFy-aRZG-R0Hd5bpDfOqk")])],"isStart":false});
            var Q12;
            Q12=makeQuery(id+"F2.opExtrude","CAP_EDGE",EDGE,{"disambiguationData":[OSD([sQuery(id+"F1.wireOp",EDGE,"z6kHnCYS-EehM-PqFy-aRZG-R0Hd5bpDfOqk")])],"isStart":true});
            var Q13;
            Q13=makeQuery(id+"F2.opExtrude","CAP_EDGE",EDGE,{"disambiguationData":[OSD([sQuery(id+"F1.wireOp",EDGE,"TqFosptJ-e80p-NSia-VRGU-4potEBLNdm0S"),sQuery(id+"F1.wireOp",EDGE,"Vc4PoYxX-D6Pj-s6fX-x5NK-R8lTQmO3Xmnw")])],"isStart":true});
            var Q14;
            Q14=makeQuery(id+"F2.opExtrude","CAP_EDGE",EDGE,{"disambiguationData":[OSD([sQuery(id+"F1.wireOp",EDGE,"15d13afc-9ba3-4549-bfcd-cc3ab7ef1af9.trimOffspring")])],"isStart":false});
            var Q15;
            Q15=makeQuery(id+"F2.opExtrude","CAP_EDGE",EDGE,{"disambiguationData":[OSD([sQuery(id+"F1.wireOp",EDGE,"E16")])],"isStart":false});
            var Q16;
            Q16=makeQuery(id+"F2.opExtrude","CAP_EDGE",EDGE,{"disambiguationData":[OSD([sQuery(id+"F1.wireOp",EDGE,"DqzT9wzE-QKBd-hKXL-xd2i-dLmxpIQpI03c")])],"isStart":false});
            var Q17;
            Q17=makeQuery(id+"F2.opExtrude","CAP_EDGE",EDGE,{"disambiguationData":[OSD([sQuery(id+"F1.wireOp",EDGE,"Aao6JbBj-ixHZ-LHBj-1GMs-VehlcfEAaExJ")])],"isStart":false});
            var Q18;
            Q18=makeQuery(id+"F2.opExtrude","CAP_EDGE",EDGE,{"disambiguationData":[OSD([sQuery(id+"F1.wireOp",EDGE,"E27.trimOffspring")])],"isStart":false});
            var Q19;
            Q19=makeQuery(id+"F2.opExtrude","CAP_EDGE",EDGE,{"disambiguationData":[OSD([sQuery(id+"F1.wireOp",EDGE,"E15")])],"isStart":false});
            var Q20;
            Q20=makeQuery(id+"F2.opExtrude","CAP_EDGE",EDGE,{"disambiguationData":[OSD([sQuery(id+"F1.wireOp",EDGE,"E14")])],"isStart":false});
            var Q21;
            Q21=makeQuery(id+"F2.opExtrude","CAP_EDGE",EDGE,{"disambiguationData":[OSD([sQuery(id+"F1.wireOp",EDGE,"E14")])],"isStart":true});
            var Q22;
            Q22=makeQuery(id+"F2.opExtrude","CAP_EDGE",EDGE,{"disambiguationData":[OSD([sQuery(id+"F1.wireOp",EDGE,"E8")])],"isStart":true});
            var Q23;
            Q23=makeQuery(id+"F2.opExtrude","CAP_EDGE",EDGE,{"disambiguationData":[OSD([sQuery(id+"F1.wireOp",EDGE,"E6")])],"isStart":true});
            var Q24;
            Q24=makeQuery(id+"F2.opExtrude","CAP_EDGE",EDGE,{"disambiguationData":[OSD([sQuery(id+"F1.wireOp",EDGE,"E15")])],"isStart":true});
            var Q25;
            Q25=makeQuery(id+"F2.opExtrude","CAP_EDGE",EDGE,{"disambiguationData":[OSD([sQuery(id+"F1.wireOp",EDGE,"E27.trimOffspring")])],"isStart":true});
            var Q26;
            Q26=makeQuery(id+"F2.opExtrude","CAP_EDGE",EDGE,{"disambiguationData":[OSD([sQuery(id+"F1.wireOp",EDGE,"Aao6JbBj-ixHZ-LHBj-1GMs-VehlcfEAaExJ")])],"isStart":true});
            var Q27;
            Q27=makeQuery(id+"F2.opExtrude","CAP_EDGE",EDGE,{"disambiguationData":[OSD([sQuery(id+"F1.wireOp",EDGE,"DqzT9wzE-QKBd-hKXL-xd2i-dLmxpIQpI03c")])],"isStart":true});
            var Q28;
            Q28=makeQuery(id+"F2.opExtrude","CAP_EDGE",EDGE,{"disambiguationData":[OSD([sQuery(id+"F1.wireOp",EDGE,"E16")])],"isStart":true});
            var Q29;
            Q29=makeQuery(id+"F2.opExtrude","CAP_EDGE",EDGE,{"disambiguationData":[OSD([sQuery(id+"F1.wireOp",EDGE,"15d13afc-9ba3-4549-bfcd-cc3ab7ef1af9.trimOffspring")])],"isStart":true});
            var Q30;
            Q30=makeQuery(id+"F2.opExtrude","CAP_EDGE",EDGE,{"disambiguationData":[OSD([sQuery(id+"F1.wireOp",EDGE,"E8")])],"isStart":false});
            var Q31;
            Q31=makeQuery(id+"F2.opExtrude","CAP_EDGE",EDGE,{"disambiguationData":[OSD([sQuery(id+"F1.wireOp",EDGE,"E6")])],"isStart":false});
            var Q32;
            Q32=makeQuery(id+"F2.opExtrude","CAP_EDGE",EDGE,{"disambiguationData":[OSD([sQuery(id+"F1.wireOp",EDGE,"E45")])],"isStart":true});
            var Q33;
            Q33=makeQuery(id+"F2.opExtrude","CAP_EDGE",EDGE,{"disambiguationData":[OSD([sQuery(id+"F1.wireOp",EDGE,"E44")])],"isStart":true});
            var Q34;
            Q34=makeQuery(id+"F2.opExtrude","CAP_EDGE",EDGE,{"disambiguationData":[OSD([sQuery(id+"F1.wireOp",EDGE,"E43")])],"isStart":true});
            var Q35;
            Q35=makeQuery(id+"F2.opExtrude","CAP_EDGE",EDGE,{"disambiguationData":[OSD([sQuery(id+"F1.wireOp",EDGE,"E42")])],"isStart":true});
            var Q36;
            Q36=makeQuery(id+"F2.opExtrude","CAP_EDGE",EDGE,{"disambiguationData":[OSD([sQuery(id+"F1.wireOp",EDGE,"E46")])],"isStart":true});
            var Q37;
            Q37=makeQuery(id+"F2.opExtrude","CAP_EDGE",EDGE,{"disambiguationData":[OSD([sQuery(id+"F1.wireOp",EDGE,"E40")])],"isStart":true});
            var Q38;
            Q38=makeQuery(id+"F2.opExtrude","CAP_EDGE",EDGE,{"disambiguationData":[OSD([sQuery(id+"F1.wireOp",EDGE,"E39")])],"isStart":true});
            var Q39;
            Q39=makeQuery(id+"F2.opExtrude","CAP_EDGE",EDGE,{"disambiguationData":[OSD([sQuery(id+"F1.wireOp",EDGE,"E47")])],"isStart":true});
            var Q40;
            Q40=makeQuery(id+"F2.opExtrude","CAP_EDGE",EDGE,{"disambiguationData":[OSD([sQuery(id+"F1.wireOp",EDGE,"E48")])],"isStart":true});
            var Q41;
            Q41=makeQuery(id+"F2.opExtrude","CAP_EDGE",EDGE,{"disambiguationData":[OSD([sQuery(id+"F1.wireOp",EDGE,"E49")])],"isStart":true});
            var Q42;
            Q42=makeQuery(id+"F2.opExtrude","CAP_EDGE",EDGE,{"disambiguationData":[OSD([sQuery(id+"F1.wireOp",EDGE,"E34.trimOffspring"),sQuery(id+"F1.wireOp",EDGE,"E37")])],"isStart":true});
            var Q43;
            Q43=makeQuery(id+"F2.opExtrude","CAP_EDGE",EDGE,{"disambiguationData":[OSD([sQuery(id+"F1.wireOp",EDGE,"E56.0")])],"isStart":true});
            var Q44;
            Q44=makeQuery(id+"F2.opExtrude","CAP_EDGE",EDGE,{"disambiguationData":[OSD([sQuery(id+"F1.wireOp",EDGE,"E34.trimOffspring"),sQuery(id+"F1.wireOp",EDGE,"E37")])],"isStart":false});
            var Q45;
            Q45=makeQuery(id+"F2.opExtrude","CAP_EDGE",EDGE,{"disambiguationData":[OSD([sQuery(id+"F1.wireOp",EDGE,"E49")])],"isStart":false});
            var Q46;
            Q46=makeQuery(id+"F2.opExtrude","CAP_EDGE",EDGE,{"disambiguationData":[OSD([sQuery(id+"F1.wireOp",EDGE,"E48")])],"isStart":false});
            var Q47;
            Q47=makeQuery(id+"F2.opExtrude","CAP_EDGE",EDGE,{"disambiguationData":[OSD([sQuery(id+"F1.wireOp",EDGE,"E47")])],"isStart":false});
            var Q48;
            Q48=makeQuery(id+"F2.opExtrude","CAP_EDGE",EDGE,{"disambiguationData":[OSD([sQuery(id+"F1.wireOp",EDGE,"E39")])],"isStart":false});
            var Q49;
            Q49=makeQuery(id+"F2.opExtrude","CAP_EDGE",EDGE,{"disambiguationData":[OSD([sQuery(id+"F1.wireOp",EDGE,"E40")])],"isStart":false});
            var Q50;
            Q50=makeQuery(id+"F2.opExtrude","CAP_EDGE",EDGE,{"disambiguationData":[OSD([sQuery(id+"F1.wireOp",EDGE,"E46")])],"isStart":false});
            var Q51;
            Q51=makeQuery(id+"F2.opExtrude","CAP_EDGE",EDGE,{"disambiguationData":[OSD([sQuery(id+"F1.wireOp",EDGE,"E42")])],"isStart":false});
            var Q52;
            Q52=makeQuery(id+"F2.opExtrude","CAP_EDGE",EDGE,{"disambiguationData":[OSD([sQuery(id+"F1.wireOp",EDGE,"E43")])],"isStart":false});
            var Q53;
            Q53=makeQuery(id+"F2.opExtrude","CAP_EDGE",EDGE,{"disambiguationData":[OSD([sQuery(id+"F1.wireOp",EDGE,"E44")])],"isStart":false});
            var Q54;
            Q54=makeQuery(id+"F2.opExtrude","CAP_EDGE",EDGE,{"disambiguationData":[OSD([sQuery(id+"F1.wireOp",EDGE,"E45")])],"isStart":false});
            var Q55;
            Q55=makeQuery(id+"F2.opExtrude","CAP_EDGE",EDGE,{"disambiguationData":[OSD([sQuery(id+"F1.wireOp",EDGE,"E56.0")])],"isStart":false});
            chamfer(context, id + "F12", {"entities" : qUnion([Q0, Q1, Q2, Q3, Q4, Q5, Q6, Q7, Q8, Q9, Q10, Q11, Q12, Q13, Q14, Q15, Q16, Q17, Q18, Q19, Q20, Q21, Q22, Q23, Q24, Q25, Q26, Q27, Q28, Q29, Q30, Q31, Q32, Q33, Q34, Q35, Q36, Q37, Q38, Q39, Q40, Q41, Q42, Q43, Q44, Q45, Q46, Q47, Q48, Q49, Q50, Q51, Q52, Q53, Q54, Q55]), "width" : 1 * mm, "tangentPropagation" : true});
        }
        {
            var Q0;
            Q0=makeQuery(id+"F10.boolean.opBoolean","COPY",FACE,{"derivedFrom":makeQuery(id+"F10.opExtrude","SWEPT_FACE",FACE,{"disambiguationData":[OSD([sQuery(id+"F9.wireOp",EDGE,"E115")])]})});
            var sketch = newSketch(context, id + "F13", { "sketchPlane" : qUnion([Q0])});
            skLineSegment(sketch, "E117.0", {"start": v(0, 8.81) * mm, "end": v(0, 1.81) * mm, "construction": true});
            skLineSegment(sketch, "E118", {"start": v(0, 5.31) * mm, "end": v(-7, 5.31) * mm, "construction": true});
            skArc(sketch, "E119", {"start": v(-3.5, 7.81) * mm, "mid": v(-6, 5.31) * mm, "end": v(-3.5, 2.81) * mm});
            skLineSegment(sketch, "E120", {"start": v(-3.5, 5.31) * mm, "end": v(-3.5, 7.81) * mm, "construction": true});
            skLineSegment(sketch, "E121", {"start": v(-3.5, 7.81) * mm, "end": v(0, 7.81) * mm});
            skLineSegment(sketch, "E122.MirrorCS", {"start": v(-3.5, 2.81) * mm, "end": v(0, 2.81) * mm});
            skSolve(sketch);
        }
        {
            var Q0;
            Q0=makeQuery(id+"F13.imprint","IMPRINT",FACE,{"disambiguationData":[TD([[makeQuery(id+"F13.imprint","IMPRINT",EDGE,{"derivedFrom":sQuery(id+"F13.wireOp",EDGE,"E119")}),1.0]])]});
            extrude(context, id + "F14", {"entities" : qUnion([Q0]), "operationType" : NewBodyOperationType.REMOVE, "oppositeDirection" : true, "depth" : 25 * mm, "offsetDistance" : 25 * mm});
        }
        {
            var Q0;
            Q0=makeQuery(id+"F14.boolean.opBoolean","INTERSECT",EDGE,{"derivedFrom":[makeQuery(id+"F2.opExtrude","SWEPT_FACE",FACE,{"disambiguationData":[OSD([sQuery(id+"F1.wireOp",EDGE,"XXJIcc4o-OTew-1mbU-SmsV-49a9MDvK9wcg")])]}),makeQuery(id+"F14.opExtrude","SWEPT_FACE",FACE,{"disambiguationData":[OSD([sQuery(id+"F13.wireOp",EDGE,"E119")])]})]});
            var Q1;
            Q1=makeQuery(id+"F14.boolean.opBoolean","COPY",EDGE,{"derivedFrom":makeQuery(id+"F14.opExtrude","SWEPT_EDGE",EDGE,{"disambiguationData":[OSD([sQuery(id+"F9.wireOp",EDGE,"E115"),sQuery(id+"F13.wireOp",EDGE,"E122.MirrorCS")])]})});
            var Q2;
            Q2=makeQuery(id+"F14.boolean.opBoolean","COPY",EDGE,{"derivedFrom":makeQuery(id+"F14.opExtrude","SWEPT_EDGE",EDGE,{"disambiguationData":[OSD([sQuery(id+"F9.wireOp",EDGE,"E115"),sQuery(id+"F13.wireOp",EDGE,"E121")])]})});
            var Q3;
            Q3=makeQuery(id+"F10.boolean.opBoolean","COPY",EDGE,{"derivedFrom":makeQuery(id+"F10.opExtrude","CAP_EDGE",EDGE,{"disambiguationData":[OSD([sQuery(id+"F1.wireOp",EDGE,"E7")])],"isStart":false})});
            var Q4;
            Q4=makeQuery(id+"F10.boolean.opBoolean","COPY",EDGE,{"derivedFrom":makeQuery(id+"F10.opExtrude","SWEPT_EDGE",EDGE,{"disambiguationData":[OSD([sQuery(id+"F1.wireOp",EDGE,"E7"),sQuery(id+"F9.wireOp",EDGE,"E114")])]})});
            var Q5;
            Q5=makeQuery(id+"F10.boolean.opBoolean","COPY",EDGE,{"derivedFrom":makeQuery(id+"F10.opExtrude","SWEPT_EDGE",EDGE,{"disambiguationData":[OSD([sQuery(id+"F1.wireOp",EDGE,"E7"),sQuery(id+"F9.wireOp",EDGE,"E116")])]})});
            var Q6;
            Q6=makeQuery(id+"F14.boolean.opBoolean","COPY",EDGE,{"derivedFrom":makeQuery(id+"F14.opExtrude","CAP_EDGE",EDGE,{"disambiguationData":[OSD([sQuery(id+"F13.wireOp",EDGE,"E119")])],"isStart":true})});
            fillet(context, id + "F15", {"entities" : qUnion([Q0, Q1, Q2, Q3, Q4, Q5, Q6]), "radius" : 1 * mm, "tangentPropagation" : true, "allowEdgeOverflow" : false});
        }
    });
